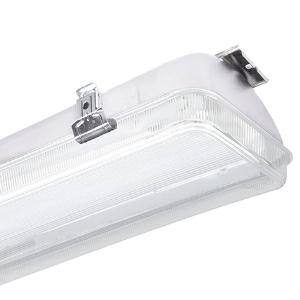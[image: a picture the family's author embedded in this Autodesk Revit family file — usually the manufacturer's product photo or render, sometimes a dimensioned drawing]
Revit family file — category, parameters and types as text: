
# Revit family: 3f_filippi_-_beta_235_75_pc_ampio_3f_filippi_-_52846_-_beta_235_led_752x45_ampio_l1265
name_source: partatom
category: Lighting Fixtures
units: mm (PartAtom-declared; Revit-internal decimal feet)

## family parameters
Cut with Voids When Loaded = No
Host = Face
Light Source = No
Part Type = Normal
Room Calculation Point = No
Round Connector Dimension = Use Diameter
Shared = No

## types (1)
- 3F Filippi - Beta 235 75 PC Ampio (1 x LED, 14369 lm, 92 W, 4000 K)
    Apparent Load = 92 VA
    Approval mark = CE
    CIE Flux Codes = 59 89 98 98 100
    Color Rendering = 80
    Color Temperature = 4000 K
    Control Gear = Electronic ballast
    Default Elevation = 1800 mm
    Description = ILLUMINOTECHNICAL
Luminous efficiency 100% (DLOR 99%, ULOR 1%).
Initial luminous flux of the luminaire 14369 lm.
Wide symmetric distribution.
Installation Interdistance Transv.D = 1.40 x hu - Long.D = 1.43 x hu.
Tabular UGR (CIE 117 - 4H-8H; S=0.25H; 70/50/20): RUG 21.3 - 21.9.
Beam angle: 98° - 100°.
Luminous efficacy 156 lm/W.
Lifetime (L93/B10): 30000 h. (tq+25°C)
Lifetime (L90/B10): 50000 h. (tq+25°C)
Lifetime (L85/B10): 80000 h. (tq+25°C)
Lifetime (L80/B10): 100000 h. (tq+25°C)
Lifetime (L85/B10): 50000 h. (tq+45°C)
Sudden decreased luminous flux after 50000 hours: 0% (C0).
Photobiological safety in compliance with IEC/TR 62778: RG0 risk exempt, (IEC 62471).
In compliance with IEC/EN 62722-2-1 - IEC/EN 62717 standards.

SOURCE
2 linear LED modules 45W/840.
Energy efficiency class (UE 2019/2020 - UE 2019/2015): C.
CIE 13.3 Colour rendering index: CRI >80 (R9 <50%).
IES TM-30 Fidelity Index: Rf = 84 Rg = 95.
CCT nominal colour temperature 4000 K.
Colour initial tolerance (MacAdam): SDCM 3.

MECHANICAL
Single-piece housing in pressed steel, powder-coated in white epoxy-polyester.
Polycarbonate screen etched internally, V2 self-extinguishing, UV stabilised, injection moulded.
Ecologic anti-aging injected sealing gasket.
Oversized gear-tray reflector unit in highly reflective white painted hot-galvanised steel.
Methacrylate (PMMA) lenses with external flat surface.
Galvanised steel snap-lock clips for diffuser mounting (safety n° 4 per fixture).
Luminaire with limited surface temperature. - D - (EN 60598-2-24)
Dimensions: 1265x235 mm, height 135 mm. Weight 7.575 kg.
IP65 protection degree.
Mechanical strength to impacts IK10 (20 joule).
Glow-wire test resistance 850°C.

ELECTRICAL
Halogen Free electronic wiring 230V-50/60Hz, power factor 0.95, THD <25%, constant output current, class I, 1 driver.
Power of the luminaire 92 W.
ENEC - CE.
Flicker: <4%.
Luminaire compliant with EN 60598-2-22 for power supply from a centralised emergency system CPSS (Central Power Supply System), not incorporated in the luminaire - high risk areas excluded. The default power and flux are 100% in AC and 100% in DC.
Ambient temperature from -20°C to +45°C.
Temperature class T6 max 85°C.
Quick connection via M20 3P connector with 9-13 mm tightening range.
Relative humidity UR: <85%.

INSTALLATION
Ceiling / Suspended / Wall.
All accessories dedicated to this product are available on the Catalog and on our website www.3F-Filippi.com.

APPLICATIONS
Suitable product for food production plants (HACCP), IFS (Food Version 6), BRC (GSFS Food Version 7).
Dry, dusty indoor environments, subject to occasional water splashes.
Industrial environments, warehouses, environments where security locks are required on all clips, e.g. prisons (on request).
Environments in which it is necessary a total protection against falling fragments (eg environments with foodstuffs or machines with moving parts or with extreme temperature changes), use luminaires with laminated glass.
Tempered glass is not immune to falling fragments from harmless and caused by shocks or exceptionally derived from the tempering process.

WARNING
Fixture not suitable for cold stores with an ambient temperature <0°C and/or relative humidity >85%.
Luminaire designed for disposal/recycling at end-of-life.
Replaceable (LED only) light source by a professional. Replaceable control gear by a professional.
    Height = 135 mm
    Lamp = 1 x LED
    Lamp Light Flux = 14369 lm
    Lamp Power = 92 W
    Lamp count = 1
    Length = 1265 mm
    Lifetime = 50000 h
    Luminous efficacy = 156 lm/W
    Manufacturer = 3F Filippi
    ModVariant = No
    Model = 3F Filippi - 52846 - Beta 235 LED 752x45 AMPIO L1265
    Mounting Place = Ceiling
    Mounting Type = Pendant
    Number of Poles = 1
    OnlyDefault = Yes
    Power Factor = 1
    Product Name = 3F Filippi - Beta 235 75 PC Ampio
    Product group = pendant luminaire
    ProductGroupID = 9
    Protection Class = Protection class I
    Protection Degree = IP 65
    RLX_Detail_Level = 1
    RLX_Emergency_Light_Flux = 0 lm
    RLX_Emergency_Type = 0
    RLX_Emergency_Type_DB = No
    RlxData = <blob elided: 90029 chars, md5=ac14388b>
    Socket = socket
    Standby Power = 0 W
    System Light Flux = 14369 lm
    System Power = 92 W
    Type Comments = Product without accessories
    Type Image = 3ffilippi_52846.jpg
    URL = http://relux.com
    VarID = ---
    Voltage = 0 V
    Weight = 0.00 kg
    Width = 235 mm

## geometry (parser evidence)
native form markers: Blend x4, Sweep x13
no freeform markers — native parametric forms only
